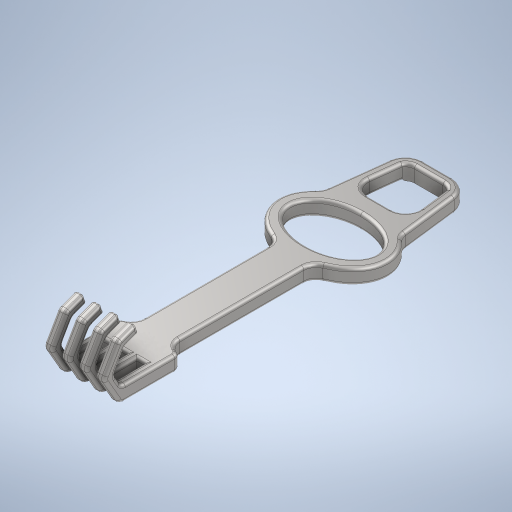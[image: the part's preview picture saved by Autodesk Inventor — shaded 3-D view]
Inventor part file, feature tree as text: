
AUTODESK INVENTOR PART (.ipt)
format: ipt  version: 2024 (Build 280153000, 153)  size: 833,024 bytes
history: native  units: mm
features: fillet x5, extrude x2, pattern_linear x1, projected_geometry x1
ambient origin geometry x8: Origin, YZ Plane, XZ Plane, XY Plane, X Axis, Y Axis, Z Axis, Center Point
bodies: Solid1 (feature_tree)
feature tree (9):
  extrude  "Extrusion1"  Depth=20.0mm
  extrude  "Extrusion2"  Depth=103.0mm
  pattern_linear  "Rectangular Pattern1"  Spacing1=8.0mm  [1 undecoded]
  fillet  "Fillet1"  Radius=20.0mm
  fillet  "Fillet2"  Radius=2.0mm
  fillet  "Fillet3"  Radius=4.0mm
  fillet  "Fillet4"  Radius=4.0mm
  fillet  "Fillet5"  Radius=25.0mm
  projected_geometry  "Projected Loop1"
note: 1 required parameter value undecoded (feature->parameter linkage not recoverable at this tier; creation-order binding heuristic only, values carry confidence <= 0.55)
